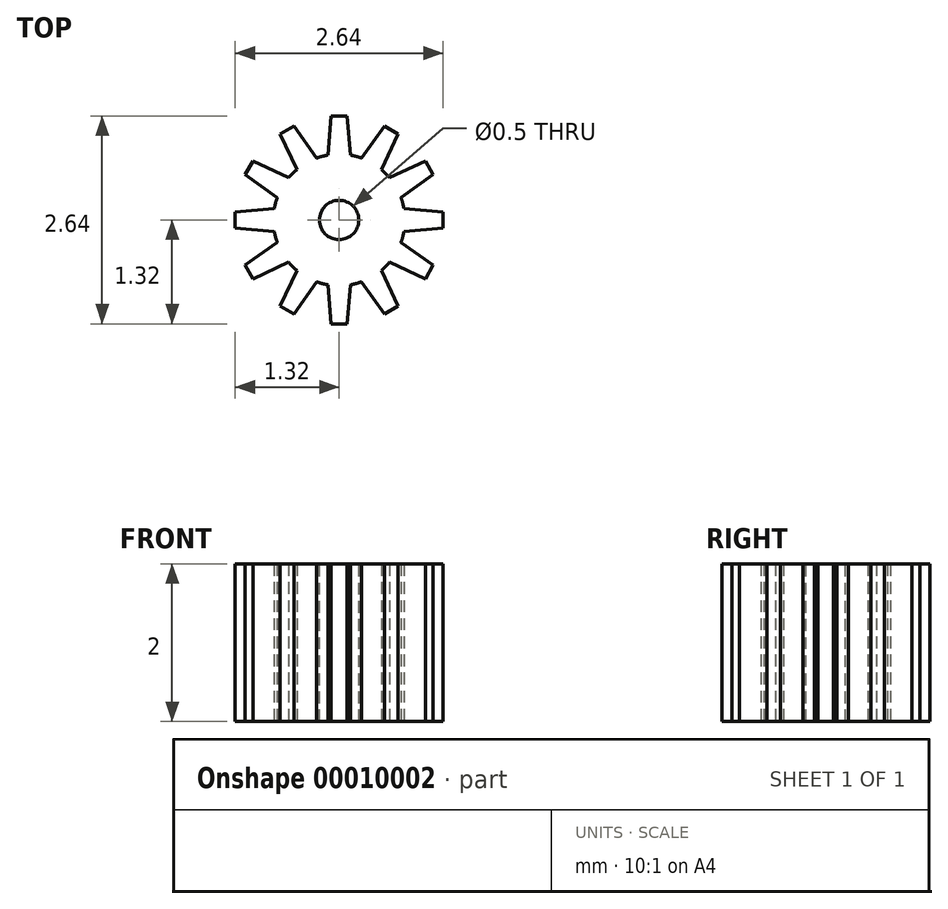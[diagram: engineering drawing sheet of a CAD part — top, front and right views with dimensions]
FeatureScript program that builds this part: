
annotation { "Feature Type Name" : "Feature", "Feature Type Description" : "" }
export const myFeature = defineFeature(function(context is Context, id is Id, definition is map)
    precondition{}
    {
        {
            var Q0;
            Q0=qCreatedBy(makeId("Top.planeOp"),FACE);
            var sketch = newSketch(context, id + "F0", { "sketchPlane" : qUnion([Q0])});
            skCircle(sketch, "E0", {"center": v(0, 0) * mm, "radius": 0.84 * mm});
            skLineSegment(sketch, "E1", {"start": v(0, 0) * mm, "end": v(0, 0.84) * mm, "construction": true});
            skLineSegment(sketch, "E2", {"start": v(-0.14, 0.82) * mm, "end": v(-0.1, 1.32) * mm});
            skLineSegment(sketch, "E3", {"start": v(-0.1, 1.32) * mm, "end": v(0, 1.32) * mm});
            skLineSegment(sketch, "E4.0.MirrorCS", {"start": v(0.1, 1.32) * mm, "end": v(0, 1.32) * mm});
            skLineSegment(sketch, "E5.0.MirrorCS", {"start": v(0.14, 0.82) * mm, "end": v(0.1, 1.32) * mm});
            skLineSegment(sketch, "E6.1.0", {"start": v(-0.54, 0.64) * mm, "end": v(-0.75, 1.1) * mm});
            skLineSegment(sketch, "E6.1.1", {"start": v(-0.75, 1.1) * mm, "end": v(-0.66, 1.14) * mm});
            skLineSegment(sketch, "E6.1.2", {"start": v(-0.57, 1.2) * mm, "end": v(-0.66, 1.14) * mm});
            skLineSegment(sketch, "E6.1.3", {"start": v(-0.29, 0.79) * mm, "end": v(-0.57, 1.2) * mm});
            skLineSegment(sketch, "E6.2.0", {"start": v(-0.79, 0.29) * mm, "end": v(-1.2, 0.57) * mm});
            skLineSegment(sketch, "E6.2.1", {"start": v(-1.2, 0.57) * mm, "end": v(-1.14, 0.66) * mm});
            skLineSegment(sketch, "E6.2.2", {"start": v(-1.1, 0.75) * mm, "end": v(-1.14, 0.66) * mm});
            skLineSegment(sketch, "E6.2.3", {"start": v(-0.64, 0.54) * mm, "end": v(-1.1, 0.75) * mm});
            skLineSegment(sketch, "E6.3.0", {"start": v(-0.82, -0.14) * mm, "end": v(-1.32, -0.1) * mm});
            skLineSegment(sketch, "E6.3.1", {"start": v(-1.32, -0.1) * mm, "end": v(-1.32, 0) * mm});
            skLineSegment(sketch, "E6.3.2", {"start": v(-1.32, 0.1) * mm, "end": v(-1.32, 0) * mm});
            skLineSegment(sketch, "E6.3.3", {"start": v(-0.82, 0.14) * mm, "end": v(-1.32, 0.1) * mm});
            skLineSegment(sketch, "E6.4.0", {"start": v(-0.64, -0.54) * mm, "end": v(-1.1, -0.75) * mm});
            skLineSegment(sketch, "E6.4.1", {"start": v(-1.1, -0.75) * mm, "end": v(-1.14, -0.66) * mm});
            skLineSegment(sketch, "E6.4.2", {"start": v(-1.2, -0.57) * mm, "end": v(-1.14, -0.66) * mm});
            skLineSegment(sketch, "E6.4.3", {"start": v(-0.79, -0.29) * mm, "end": v(-1.2, -0.57) * mm});
            skLineSegment(sketch, "E6.5.0", {"start": v(-0.29, -0.79) * mm, "end": v(-0.57, -1.2) * mm});
            skLineSegment(sketch, "E6.5.1", {"start": v(-0.57, -1.2) * mm, "end": v(-0.66, -1.14) * mm});
            skLineSegment(sketch, "E6.5.2", {"start": v(-0.75, -1.1) * mm, "end": v(-0.66, -1.14) * mm});
            skLineSegment(sketch, "E6.5.3", {"start": v(-0.54, -0.64) * mm, "end": v(-0.75, -1.1) * mm});
            skLineSegment(sketch, "E6.6.0", {"start": v(0.14, -0.82) * mm, "end": v(0.1, -1.32) * mm});
            skLineSegment(sketch, "E6.6.1", {"start": v(0.1, -1.32) * mm, "end": v(0, -1.32) * mm});
            skLineSegment(sketch, "E6.6.2", {"start": v(-0.1, -1.32) * mm, "end": v(0, -1.32) * mm});
            skLineSegment(sketch, "E6.6.3", {"start": v(-0.14, -0.82) * mm, "end": v(-0.1, -1.32) * mm});
            skLineSegment(sketch, "E6.7.0", {"start": v(0.54, -0.64) * mm, "end": v(0.75, -1.1) * mm});
            skLineSegment(sketch, "E6.7.1", {"start": v(0.75, -1.1) * mm, "end": v(0.66, -1.14) * mm});
            skLineSegment(sketch, "E6.7.2", {"start": v(0.57, -1.2) * mm, "end": v(0.66, -1.14) * mm});
            skLineSegment(sketch, "E6.7.3", {"start": v(0.29, -0.79) * mm, "end": v(0.57, -1.2) * mm});
            skLineSegment(sketch, "E6.8.0", {"start": v(0.79, -0.29) * mm, "end": v(1.2, -0.57) * mm});
            skLineSegment(sketch, "E6.8.1", {"start": v(1.2, -0.57) * mm, "end": v(1.14, -0.66) * mm});
            skLineSegment(sketch, "E6.8.2", {"start": v(1.1, -0.75) * mm, "end": v(1.14, -0.66) * mm});
            skLineSegment(sketch, "E6.8.3", {"start": v(0.64, -0.54) * mm, "end": v(1.1, -0.75) * mm});
            skLineSegment(sketch, "E6.9.0", {"start": v(0.82, 0.14) * mm, "end": v(1.32, 0.1) * mm});
            skLineSegment(sketch, "E6.9.1", {"start": v(1.32, 0.1) * mm, "end": v(1.32, 0) * mm});
            skLineSegment(sketch, "E6.9.2", {"start": v(1.32, -0.1) * mm, "end": v(1.32, 0) * mm});
            skLineSegment(sketch, "E6.9.3", {"start": v(0.82, -0.14) * mm, "end": v(1.32, -0.1) * mm});
            skLineSegment(sketch, "E6.10.0", {"start": v(0.64, 0.54) * mm, "end": v(1.1, 0.75) * mm});
            skLineSegment(sketch, "E6.10.1", {"start": v(1.1, 0.75) * mm, "end": v(1.14, 0.66) * mm});
            skLineSegment(sketch, "E6.10.2", {"start": v(1.2, 0.57) * mm, "end": v(1.14, 0.66) * mm});
            skLineSegment(sketch, "E6.10.3", {"start": v(0.79, 0.29) * mm, "end": v(1.2, 0.57) * mm});
            skLineSegment(sketch, "E6.11.0", {"start": v(0.29, 0.79) * mm, "end": v(0.57, 1.2) * mm});
            skLineSegment(sketch, "E6.11.1", {"start": v(0.57, 1.2) * mm, "end": v(0.66, 1.14) * mm});
            skLineSegment(sketch, "E6.11.2", {"start": v(0.75, 1.1) * mm, "end": v(0.66, 1.14) * mm});
            skLineSegment(sketch, "E6.11.3", {"start": v(0.54, 0.64) * mm, "end": v(0.75, 1.1) * mm});
            skSolve(sketch);
        }
        {
            var Q0;
            Q0=qSketchRegion(id+"F0",true);
            extrude(context, id + "F1", {"entities" : qUnion([Q0]), "depth" : 2 * mm});
        }
        {
            var Q0;
            Q0=makeQuery(id+"F1.opExtrude","CAP_FACE",FACE,{"disambiguationData":[OSD([sQuery(id+"F0.wireOp",EDGE,"E0"),sQuery(id+"F0.wireOp",EDGE,"E2"),sQuery(id+"F0.wireOp",EDGE,"E3"),sQuery(id+"F0.wireOp",EDGE,"E4.0.MirrorCS"),sQuery(id+"F0.wireOp",EDGE,"E5.0.MirrorCS"),sQuery(id+"F0.wireOp",EDGE,"E6.1.0"),sQuery(id+"F0.wireOp",EDGE,"E6.1.1"),sQuery(id+"F0.wireOp",EDGE,"E6.1.2"),sQuery(id+"F0.wireOp",EDGE,"E6.1.3"),sQuery(id+"F0.wireOp",EDGE,"E6.2.0"),sQuery(id+"F0.wireOp",EDGE,"E6.2.1"),sQuery(id+"F0.wireOp",EDGE,"E6.2.2"),sQuery(id+"F0.wireOp",EDGE,"E6.2.3"),sQuery(id+"F0.wireOp",EDGE,"E6.3.0"),sQuery(id+"F0.wireOp",EDGE,"E6.3.1"),sQuery(id+"F0.wireOp",EDGE,"E6.3.2"),sQuery(id+"F0.wireOp",EDGE,"E6.3.3"),sQuery(id+"F0.wireOp",EDGE,"E6.4.0"),sQuery(id+"F0.wireOp",EDGE,"E6.4.1"),sQuery(id+"F0.wireOp",EDGE,"E6.4.2"),sQuery(id+"F0.wireOp",EDGE,"E6.4.3"),sQuery(id+"F0.wireOp",EDGE,"E6.5.0"),sQuery(id+"F0.wireOp",EDGE,"E6.5.1"),sQuery(id+"F0.wireOp",EDGE,"E6.5.2"),sQuery(id+"F0.wireOp",EDGE,"E6.5.3"),sQuery(id+"F0.wireOp",EDGE,"E6.6.0"),sQuery(id+"F0.wireOp",EDGE,"E6.6.1"),sQuery(id+"F0.wireOp",EDGE,"E6.6.2"),sQuery(id+"F0.wireOp",EDGE,"E6.6.3"),sQuery(id+"F0.wireOp",EDGE,"E6.7.0"),sQuery(id+"F0.wireOp",EDGE,"E6.7.1"),sQuery(id+"F0.wireOp",EDGE,"E6.7.2"),sQuery(id+"F0.wireOp",EDGE,"E6.7.3"),sQuery(id+"F0.wireOp",EDGE,"E6.8.0"),sQuery(id+"F0.wireOp",EDGE,"E6.8.1"),sQuery(id+"F0.wireOp",EDGE,"E6.8.2"),sQuery(id+"F0.wireOp",EDGE,"E6.8.3"),sQuery(id+"F0.wireOp",EDGE,"E6.9.0"),sQuery(id+"F0.wireOp",EDGE,"E6.9.1"),sQuery(id+"F0.wireOp",EDGE,"E6.9.2"),sQuery(id+"F0.wireOp",EDGE,"E6.9.3"),sQuery(id+"F0.wireOp",EDGE,"E6.10.0"),sQuery(id+"F0.wireOp",EDGE,"E6.10.1"),sQuery(id+"F0.wireOp",EDGE,"E6.10.2"),sQuery(id+"F0.wireOp",EDGE,"E6.10.3"),sQuery(id+"F0.wireOp",EDGE,"E6.11.0"),sQuery(id+"F0.wireOp",EDGE,"E6.11.1"),sQuery(id+"F0.wireOp",EDGE,"E6.11.2"),sQuery(id+"F0.wireOp",EDGE,"E6.11.3")])],"isStart":false});
            var sketch = newSketch(context, id + "F2", { "sketchPlane" : qUnion([Q0])});
            skCircle(sketch, "E7", {"center": v(0, 0) * mm, "radius": 0.25 * mm});
            skSolve(sketch);
        }
        {
            var Q0;
            Q0=qSketchRegion(id+"F2",true);
            extrude(context, id + "F3", {"entities" : qUnion([Q0]), "operationType" : NewBodyOperationType.REMOVE, "oppositeDirection" : true, "depth" : 25 * mm});
        }
    });
